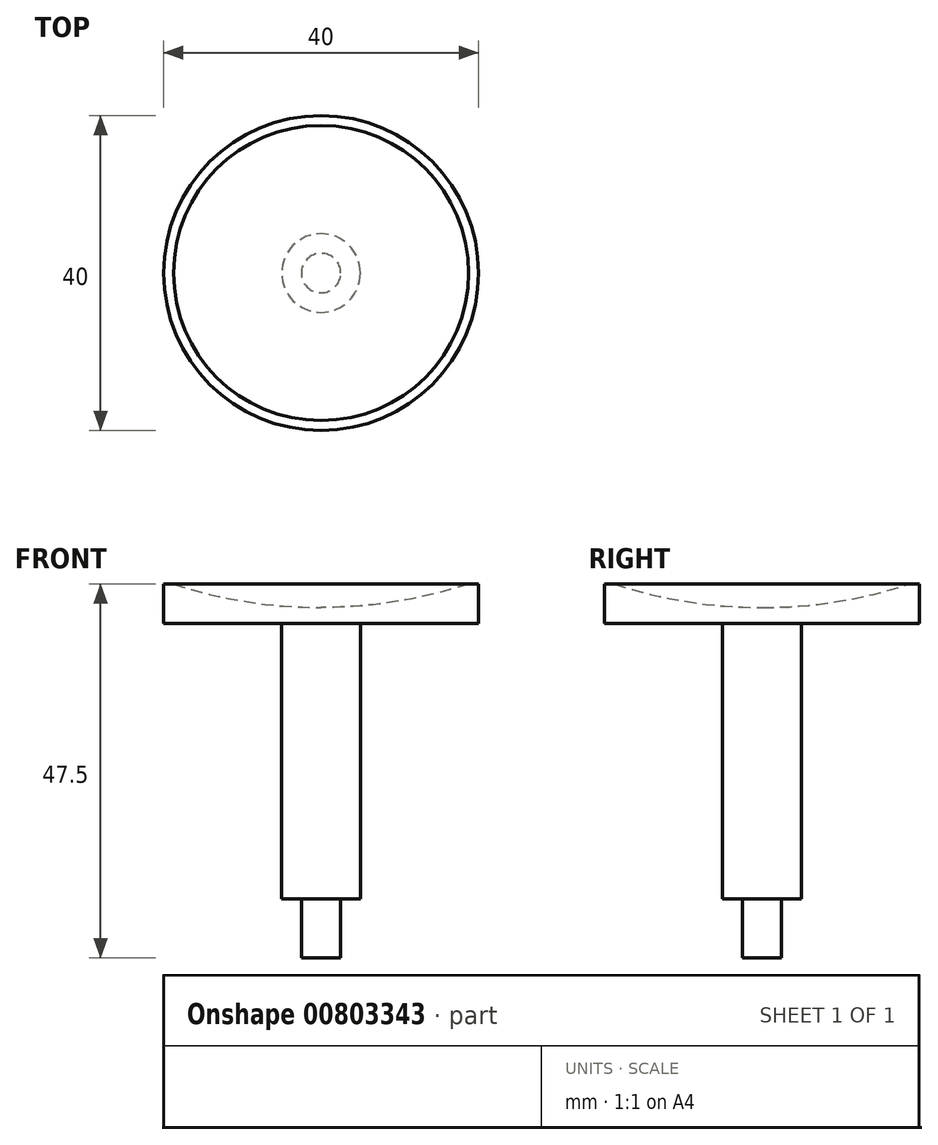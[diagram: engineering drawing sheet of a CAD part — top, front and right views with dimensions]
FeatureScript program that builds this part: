
annotation { "Feature Type Name" : "Feature", "Feature Type Description" : "" }
export const myFeature = defineFeature(function(context is Context, id is Id, definition is map)
    precondition{}
    {
        {
            var Q0;
            Q0=qCreatedBy(makeId("Front.planeOp"),FACE);
            var sketch = newSketch(context, id + "F0", { "sketchPlane" : qUnion([Q0])});
            skLineSegment(sketch, "E0.bottom", {"start": v(0, 0) * mm, "end": v(2.5, 0) * mm});
            skLineSegment(sketch, "E0.top", {"start": v(0, 35) * mm, "end": v(10, 35) * mm});
            skLineSegment(sketch, "E0.right", {"start": v(10, 0) * mm, "end": v(10, 35) * mm});
            skLineSegment(sketch, "E1.bottom", {"start": v(-15, 40) * mm, "end": v(-13.73, 40) * mm});
            skLineSegment(sketch, "E1.top", {"start": v(5, 35) * mm, "end": v(25, 35) * mm});
            skLineSegment(sketch, "E1.left", {"start": v(-15, 40) * mm, "end": v(-15, 35) * mm});
            skLineSegment(sketch, "E1.right", {"start": v(25, 40) * mm, "end": v(25, 35) * mm});
            skArc(sketch, "E2", {"start": v(5, 37) * mm, "mid": v(14.49, 37.75) * mm, "end": v(23.73, 40) * mm});
            skLineSegment(sketch, "E3.trimOffspring", {"start": v(23.73, 40) * mm, "end": v(25, 40) * mm});
            skLineSegment(sketch, "E4.bottom", {"start": v(5, -7.5) * mm, "end": v(7.5, -7.5) * mm});
            skLineSegment(sketch, "E4.right", {"start": v(7.5, -7.5) * mm, "end": v(7.5, 0) * mm});
            skLineSegment(sketch, "E5", {"start": v(5, -7.5) * mm, "end": v(5, 37) * mm});
            skLineSegment(sketch, "E6.trimOffspring", {"start": v(7.5, 0) * mm, "end": v(10, 0) * mm});
            skPoint(sketch, "E7.orphan", {"position": v(2.5, -7.5) * mm});
            skSolve(sketch);
        }
        {
            var Q0;
            {var subQ1=sQuery(id+"F0.wireOp",EDGE,"E1.top");var subQ5=sQuery(id+"F0.wireOp",EDGE,"E0.right");Q0=qUnion([makeQuery(id+"F0.imprint","IMPRINT",FACE,{"disambiguationData":[TD([[makeQuery(id+"F0.imprint","IMPRINT",EDGE,{"derivedFrom":subQ5}),1.0]])]}),makeQuery(id+"F0.imprint","IMPRINT",FACE,{"disambiguationData":[TD([[makeQuery(id+"F0.imprint","IMPRINT",EDGE,{"derivedFrom":subQ1}),1.0]])]})]);}
            var Q1;
            Q1=sQuery(id+"F0.wireOp",EDGE,"E5");
            revolve(context, id + "F1", {"surfaceOperationType" : NewSurfaceOperationType.NEW, "entities" : qUnion([Q0]), "axis" : qUnion([Q1]), "revolveType" : RevolveType.FULL});
        }
    });
